# Revit family: 2060770(n) 300
name_source: partatom
category: Security Devices
units: mm (PartAtom-declared; Revit-internal decimal feet)

## family parameters
Always vertical = No
Cut with Voids When Loaded = No
Host = Wall
OmniClass Number = 23.85.30.14
OmniClass Title = Presence Detection/Registration
Room Calculation Point = No
Shared = Yes

## types (2) — shared parameters
zero-valued in all types: A

## per-type parameters (varying)
- Type 1: CTN=0; EF000008=0 mm  [stored 0 ft]; EF000040=0 mm  [stored 0 ft]; EF000049=0 mm  [stored 0 ft]; EF000194=0; EF000218=0 mm  [stored 0 ft]; EF000551=0 mm  [stored 0 ft]; EF000846=0 mm  [stored 0 ft]; EF001322=0 mm  [stored 0 ft]; EF001323=0 mm  [stored 0 ft]; EF003843=0 mm  [stored 0 ft]; EF003882=0; EF004101=0.00°; EF008011=0 mm  [stored 0 ft]; EF010517=0 mm  [stored 0 ft]; EF010886=0 mm  [stored 0 ft]; EF011019=0 mm  [stored 0 ft]; EF011020=0 mm  [stored 0 ft]; EF012278=0 mm  [stored 0 ft]; EF021270=0; EF021271=0; LOG=0; NOCUPEROU=0; PRICEQUANTITY=0; QUANTITYINT=0; QUANTITYMIN=0
- 2060770: ARTICLENO=NB; BOMINFO=LINA; CATALOG=Theben; COO=CN; CTN=85365080; DEEPLINK_PRODUKTSEITE=http://www.theben.de; DESCLONG=Passive infrared motion detector for flush-mounted wall mounting, 1 channel light (2-wire version in combination with an ELPA staircase lighting timer for switching lamp loads), without cover frame, cover frame for integration into common switch programs available as accessory, semicircular detection area 170° up to 14x17 m, Automatic presence and brightness-dependent control for lighting, brightness switching value adjustable, teach-in function, pulse function, switch-on delay and follow-up time adjustable, limitation of detection range possible, integrated pushbutton (can be blocked), extension of detection range by parallel connection; DESCSHORT=Motion detector wall mounting, light, without frame; EF000003=EV000383; EF000007=White; EF000008=68 mm; EF000010=Motion detector; EF000025=false; EF000040=68 mm; EF000049=50 mm  [stored 0.164042 ft]; EF000124=Plug-in clamp; EF000139=Untreated; EF000147=false; EF000187=AC; EF000194=1800; EF000218=40 mm  [stored 0.131234 ft]; EF000416=50, 60 Hz; EF000483=false; EF000551=54 mm  [stored 0.177165 ft]; EF000846=68 mm; EF001098=true; EF001099=false; EF001198=false; EF001257=Thermoplast; EF001322=17000 mm  [stored 55.7743 ft]; EF001323=7000 mm; EF001731=-15, 45 °C; EF002169=Plastic; EF003429=true; EF003808=false; EF003814=5, 1000 lx; EF003832=false; EF003843=17000 mm  [stored 55.7743 ft]; EF003848=false; EF003858=false; EF003863=false; EF003876=false; EF003882=9010; EF003890=false; EF003898=true; EF003904=true; EF003920=false; EF004101=170.00°; EF004293=IK04; EF005474=IP20; EF005624=false; EF006243=false; EF006311=false; EF006569=shiny; EF006582=0, 170 °; EF006644=true; EF007575=true; EF008011=1200 mm; EF009569=false; EF010517=20 mm  [stored 0.0656168 ft]; EF010886=10 mm  [stored 0.0328084 ft]; EF011019=45 mm  [stored 0.147638 ft]; EF011020=50 mm  [stored 0.164042 ft]; EF011072=false; EF011991=false; EF012278=35 mm  [stored 0.114829 ft]; EF014925=false; EF014926=false; EF014927=false; EF020270=Passive infrared; EF021180=false; EF021270=85; EF021271=85; EF023790=false; GEBRAUCHSANLEITUNG=http://www.theben.de; INTNO=4003468200186; LINA=2060770; LOG=300; MANUID=2060770; MANUNAME=Theben AG; MANUTYPEDESC=theMura S180-100 2W B UP; Manufacturer=Theben; Model=2060770; NB=2060770(N) 300; NBSYN=$MANUID.($SA.) $LOG.; NN=Motion detector 230 V; NOCUPEROU=1; PRICEQUANTITY=1; PRODUKTDATENBLATT=http://www.theben.de; QUANTITYINT=1; QUANTITYMIN=1; REACH_ERKLAERUNG=http://www.theben.de; REMARKS=ERP-GROUP 450; SA=None; SUPPLIER=THEBEN; SUPPLIERALTNO=2060770

note: [stored X ft] marks values corroborated as IEEE doubles in the binary element streams (Revit-internal decimal feet)

## geometry (parser evidence)
native form markers: Sweep x12
no freeform markers — native parametric forms only
